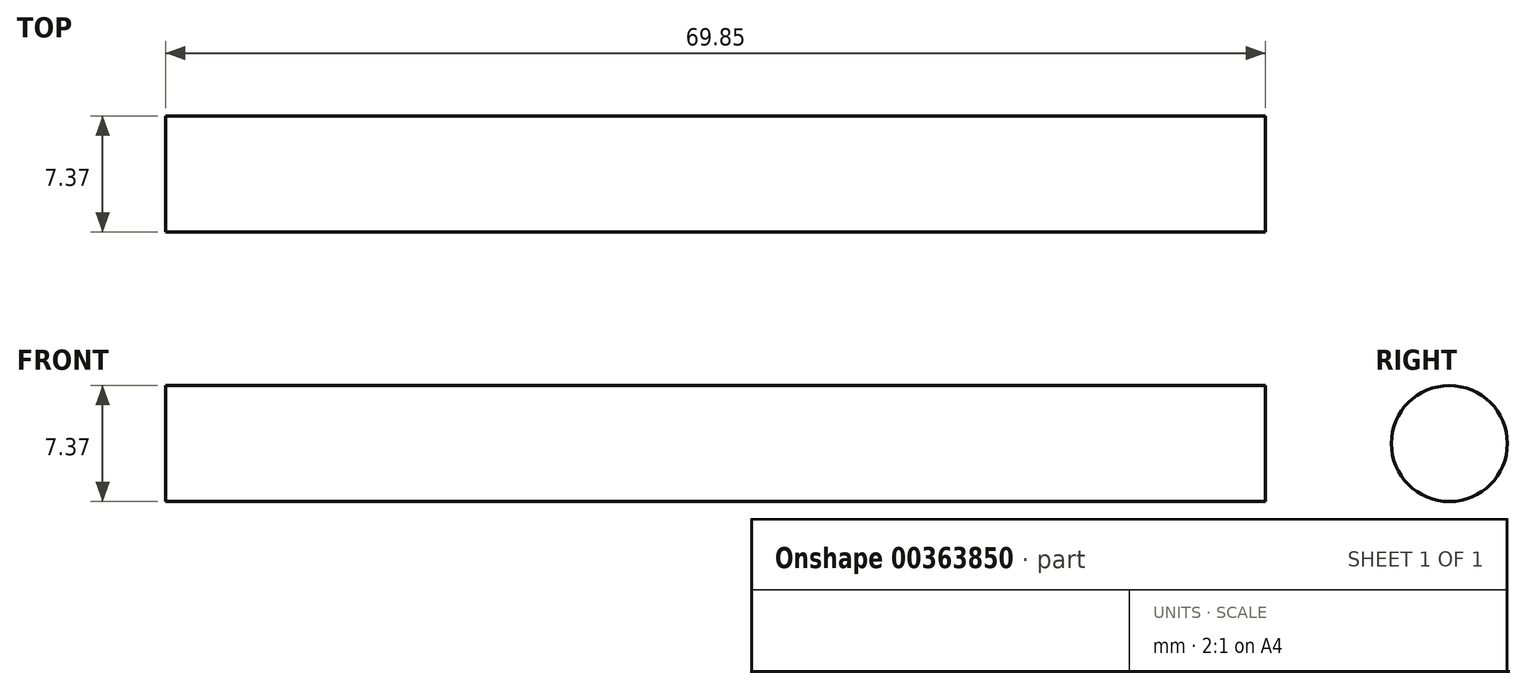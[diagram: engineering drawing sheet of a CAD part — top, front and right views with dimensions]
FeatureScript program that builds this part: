
annotation { "Feature Type Name" : "Feature", "Feature Type Description" : "" }
export const myFeature = defineFeature(function(context is Context, id is Id, definition is map)
    precondition{}
    {
        {
            var Q0;
            Q0=qCreatedBy(makeId("Right.planeOp"),FACE);
            var sketch = newSketch(context, id + "F0", { "sketchPlane" : qUnion([Q0])});
            skCircle(sketch, "E0", {"center": v(-26.56, 32.51) * mm, "radius": 3.68 * mm});
            skCircle(sketch, "E1", {"center": v(34.84, 34.29) * mm, "radius": 3.68 * mm});
            skSolve(sketch);
        }
        {
            var Q0;
            Q0=makeQuery(id+"F0.imprint","IMPRINT",FACE,{"disambiguationData":[TD([[makeQuery(id+"F0.imprint","IMPRINT",EDGE,{"derivedFrom":sQuery(id+"F0.wireOp",EDGE,"E0")}),1.0]])]});
            extrude(context, id + "F1", {"entities" : qUnion([Q0]), "depth" : 69.85 * mm});
        }
        {
            var Q0;
            Q0=sQuery(id+"F0.wireOp",EDGE,"E1");
            extrude(context, id + "F2", {"bodyType" : ToolBodyType.SURFACE, "surfaceEntities" : qUnion([Q0]), "depth" : 76.2 * mm});
        }
    });
